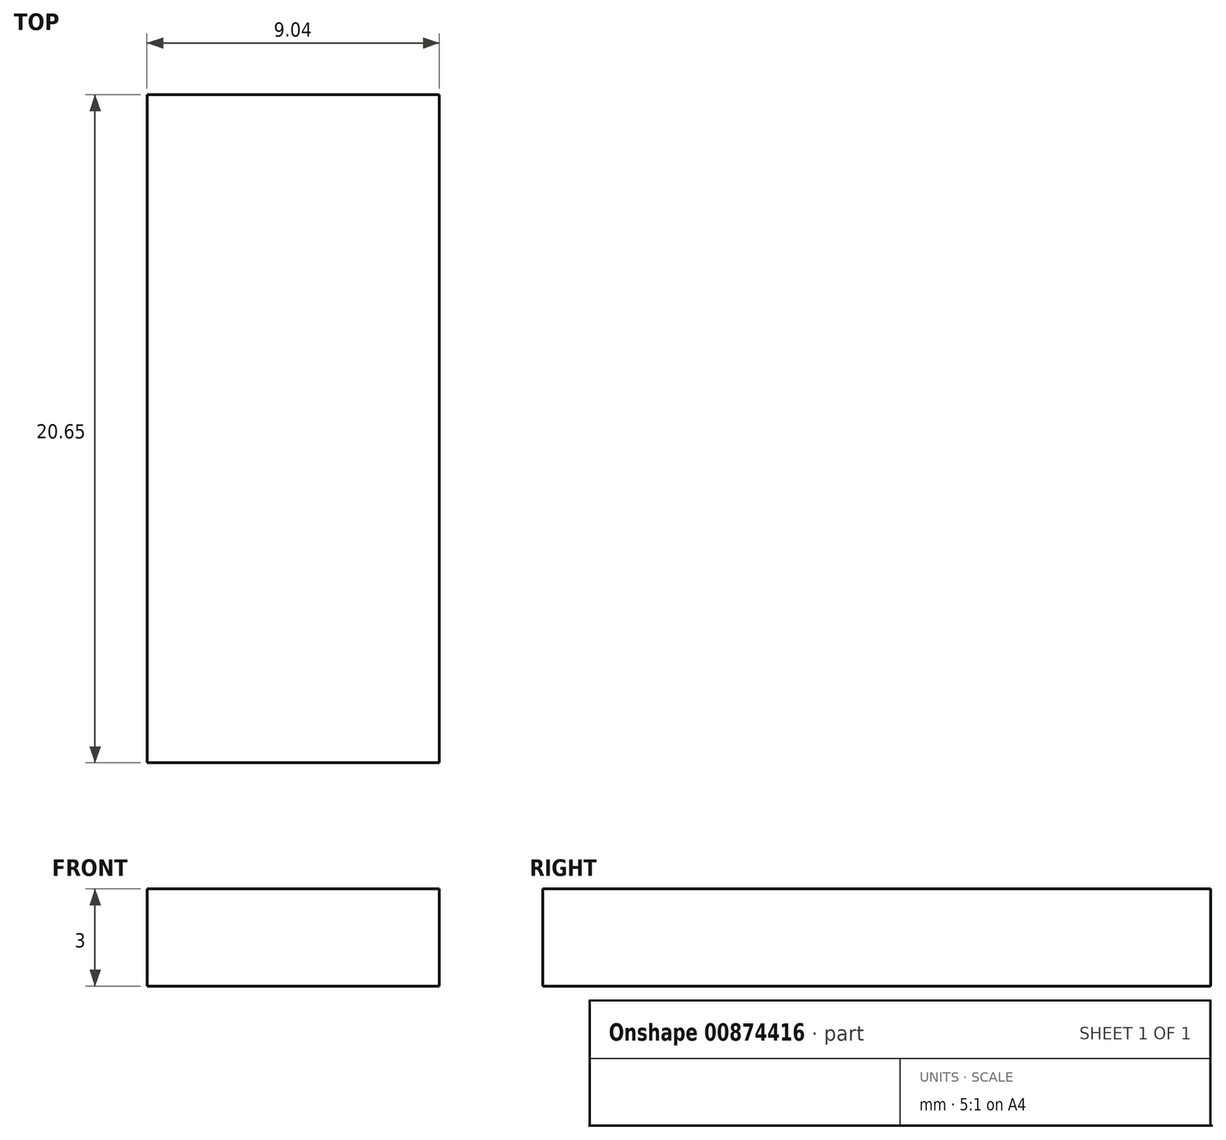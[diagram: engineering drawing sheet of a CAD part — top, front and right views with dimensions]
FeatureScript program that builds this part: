
annotation { "Feature Type Name" : "Feature", "Feature Type Description" : "" }
export const myFeature = defineFeature(function(context is Context, id is Id, definition is map)
    precondition{}
    {
        {
            var Q0;
            Q0=qCreatedBy(makeId("Top.planeOp"),FACE);
            var sketch = newSketch(context, id + "F0", { "sketchPlane" : qUnion([Q0])});
            skLineSegment(sketch, "E0.bottom", {"start": v(-24.89, 7.65) * mm, "end": v(-15.85, 7.65) * mm});
            skLineSegment(sketch, "E0.top", {"start": v(-24.89, -13) * mm, "end": v(-15.85, -13) * mm});
            skLineSegment(sketch, "E0.left", {"start": v(-24.89, 7.65) * mm, "end": v(-24.89, -13) * mm});
            skLineSegment(sketch, "E0.right", {"start": v(-15.85, 7.65) * mm, "end": v(-15.85, -13) * mm});
            skSolve(sketch);
        }
        {
            var Q0;
            Q0=makeQuery(id+"F0.imprint","IMPRINT",FACE,{"disambiguationData":[TD([[makeQuery(id+"F0.imprint","IMPRINT",EDGE,{"derivedFrom":sQuery(id+"F0.wireOp",EDGE,"E0.bottom")}),-1.0]])]});
            extrude(context, id + "F1", {"entities" : qUnion([Q0]), "depth" : 3 * mm, "offsetDistance" : 25 * mm});
        }
    });
